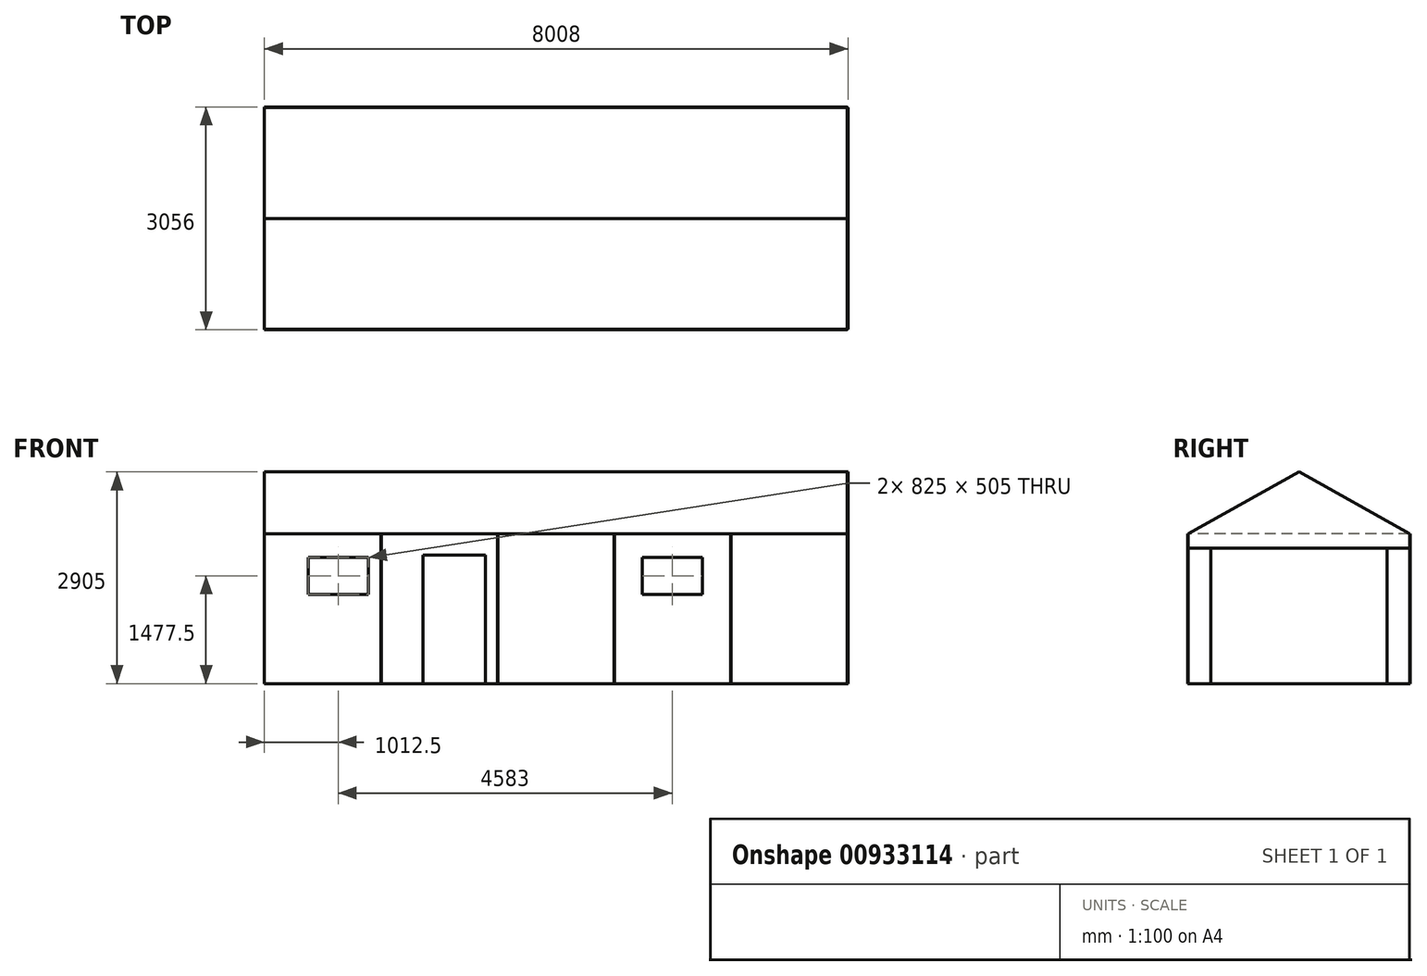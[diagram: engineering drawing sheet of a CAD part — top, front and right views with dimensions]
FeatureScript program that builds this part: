
annotation { "Feature Type Name" : "Feature", "Feature Type Description" : "" }
export const myFeature = defineFeature(function(context is Context, id is Id, definition is map)
    precondition{}
    {
        {
            var Q0;
            Q0=qCreatedBy(makeId("Top.planeOp"),FACE);
            var sketch = newSketch(context, id + "F0", { "sketchPlane" : qUnion([Q0])});
            skLineSegment(sketch, "E0.bottom", {"start": v(-4000, 1520) * mm, "end": v(4000, 1520) * mm});
            skLineSegment(sketch, "E0.top", {"start": v(-4000, -1520) * mm, "end": v(4000, -1520) * mm});
            skLineSegment(sketch, "E0.left", {"start": v(-4000, 1520) * mm, "end": v(-4000, -1520) * mm});
            skLineSegment(sketch, "E0.right", {"start": v(4000, 1520) * mm, "end": v(4000, -1520) * mm});
            skPoint(sketch, "E0.middle", {"position": v(0, 0) * mm});
            skSolve(sketch);
        }
        {
            var Q0;
            Q0 = qSketchRegion(id + "F0", true);
            extrude(context, id + "F1", {"entities" : qUnion([Q0]), "depth" : 2055 * mm, "offsetDistance" : 25 * mm});
        }
        {
            var Q0;
            Q0=makeQuery(id+"F1.opExtrude","SWEPT_FACE",FACE,{"disambiguationData":[OSD([sQuery(id+"F0.wireOp",EDGE,"E0.top")])]});
            var sketch = newSketch(context, id + "F2", { "sketchPlane" : qUnion([Q0])});
            skLineSegment(sketch, "E1.bottom", {"start": v(4000, 0) * mm, "end": v(2404, 0) * mm});
            skLineSegment(sketch, "E1.top", {"start": v(4000, 2055) * mm, "end": v(2404, 2055) * mm});
            skLineSegment(sketch, "E1.left", {"start": v(4000, 0) * mm, "end": v(4000, 2055) * mm});
            skLineSegment(sketch, "E1.right", {"start": v(2404, 0) * mm, "end": v(2404, 2055) * mm});
            skLineSegment(sketch, "E2.bottom", {"start": v(2399, 0) * mm, "end": v(803, 0) * mm});
            skLineSegment(sketch, "E2.top", {"start": v(2399, 2055) * mm, "end": v(803, 2055) * mm});
            skLineSegment(sketch, "E2.left", {"start": v(2399, 0) * mm, "end": v(2399, 2055) * mm});
            skLineSegment(sketch, "E2.right", {"start": v(803, 0) * mm, "end": v(803, 2055) * mm});
            skLineSegment(sketch, "E3.bottom", {"start": v(798, 0) * mm, "end": v(-798, 0) * mm});
            skLineSegment(sketch, "E3.top", {"start": v(798, 2055) * mm, "end": v(-798, 2055) * mm});
            skLineSegment(sketch, "E3.left", {"start": v(798, 0) * mm, "end": v(798, 2055) * mm});
            skLineSegment(sketch, "E3.right", {"start": v(-798, 0) * mm, "end": v(-798, 2055) * mm});
            skLineSegment(sketch, "E4.bottom", {"start": v(-803, 0) * mm, "end": v(-2399, 0) * mm});
            skLineSegment(sketch, "E4.top", {"start": v(-803, 2055) * mm, "end": v(-2399, 2055) * mm});
            skLineSegment(sketch, "E4.left", {"start": v(-803, 0) * mm, "end": v(-803, 2055) * mm});
            skLineSegment(sketch, "E4.right", {"start": v(-2399, 0) * mm, "end": v(-2399, 2055) * mm});
            skLineSegment(sketch, "E5.bottom", {"start": v(-2404, 0) * mm, "end": v(-4000, 0) * mm});
            skLineSegment(sketch, "E5.top", {"start": v(-2404, 2055) * mm, "end": v(-4000, 2055) * mm});
            skLineSegment(sketch, "E5.left", {"start": v(-2404, 0) * mm, "end": v(-2404, 2055) * mm});
            skLineSegment(sketch, "E5.right", {"start": v(-4000, 0) * mm, "end": v(-4000, 2055) * mm});
            skSolve(sketch);
        }
        {
            var Q0;
            Q0 = qSketchRegion(id + "F2", true);
            extrude(context, id + "F3", {"entities" : qUnion([Q0]), "depth" : 8 * mm, "offsetDistance" : 25 * mm});
        }
        {
            var Q0;
            Q0=makeQuery(id+"F1.opExtrude","SWEPT_FACE",FACE,{"disambiguationData":[OSD([sQuery(id+"F0.wireOp",EDGE,"E0.right")])]});
            var sketch = newSketch(context, id + "F4", { "sketchPlane" : qUnion([Q0])});
            skLineSegment(sketch, "E6.bottom", {"start": v(-1520, 0) * mm, "end": v(-1210, 0) * mm});
            skLineSegment(sketch, "E6.top", {"start": v(-1520, 1860) * mm, "end": v(-1210, 1860) * mm});
            skLineSegment(sketch, "E6.left", {"start": v(-1520, 0) * mm, "end": v(-1520, 1860) * mm});
            skLineSegment(sketch, "E6.right", {"start": v(-1210, 0) * mm, "end": v(-1210, 1860) * mm});
            skLineSegment(sketch, "E7.bottom", {"start": v(1520, 0) * mm, "end": v(1210, 0) * mm});
            skLineSegment(sketch, "E7.top", {"start": v(1520, 1860) * mm, "end": v(1210, 1860) * mm});
            skLineSegment(sketch, "E7.left", {"start": v(1520, 0) * mm, "end": v(1520, 1860) * mm});
            skLineSegment(sketch, "E7.right", {"start": v(1210, 0) * mm, "end": v(1210, 1860) * mm});
            skSolve(sketch);
        }
        {
            var Q0;
            Q0 = qSketchRegion(id + "F4", true);
            extrude(context, id + "F5", {"entities" : qUnion([Q0]), "depth" : 8 * mm, "offsetDistance" : 25 * mm});
        }
        {
            var Q0;
            Q0=makeQuery(id+"F1.opExtrude","SWEPT_FACE",FACE,{"disambiguationData":[OSD([sQuery(id+"F0.wireOp",EDGE,"E0.bottom")])]});
            var sketch = newSketch(context, id + "F6", { "sketchPlane" : qUnion([Q0])});
            skLineSegment(sketch, "E8.bottom", {"start": v(-4000, 0) * mm, "end": v(-2404, 0) * mm});
            skLineSegment(sketch, "E8.top", {"start": v(-4000, 2055) * mm, "end": v(-2404, 2055) * mm});
            skLineSegment(sketch, "E8.left", {"start": v(-4000, 0) * mm, "end": v(-4000, 2055) * mm});
            skLineSegment(sketch, "E8.right", {"start": v(-2404, 0) * mm, "end": v(-2404, 2055) * mm});
            skLineSegment(sketch, "E9.bottom", {"start": v(-2399, 0) * mm, "end": v(-803, 0) * mm});
            skLineSegment(sketch, "E9.top", {"start": v(-2399, 2055) * mm, "end": v(-803, 2055) * mm});
            skLineSegment(sketch, "E9.left", {"start": v(-2399, 0) * mm, "end": v(-2399, 2055) * mm});
            skLineSegment(sketch, "E9.right", {"start": v(-803, 0) * mm, "end": v(-803, 2055) * mm});
            skLineSegment(sketch, "E10.bottom", {"start": v(-798, 0) * mm, "end": v(798, 0) * mm});
            skLineSegment(sketch, "E10.top", {"start": v(-798, 2055) * mm, "end": v(798, 2055) * mm});
            skLineSegment(sketch, "E10.left", {"start": v(-798, 0) * mm, "end": v(-798, 2055) * mm});
            skLineSegment(sketch, "E10.right", {"start": v(798, 0) * mm, "end": v(798, 2055) * mm});
            skLineSegment(sketch, "E11.bottom", {"start": v(803, 0) * mm, "end": v(2399, 0) * mm});
            skLineSegment(sketch, "E11.top", {"start": v(803, 2055) * mm, "end": v(2399, 2055) * mm});
            skLineSegment(sketch, "E11.left", {"start": v(803, 0) * mm, "end": v(803, 2055) * mm});
            skLineSegment(sketch, "E11.right", {"start": v(2399, 0) * mm, "end": v(2399, 2055) * mm});
            skLineSegment(sketch, "E12.bottom", {"start": v(2404, 0) * mm, "end": v(4000, 0) * mm});
            skLineSegment(sketch, "E12.top", {"start": v(2404, 2055) * mm, "end": v(4000, 2055) * mm});
            skLineSegment(sketch, "E12.left", {"start": v(2404, 0) * mm, "end": v(2404, 2055) * mm});
            skLineSegment(sketch, "E12.right", {"start": v(4000, 0) * mm, "end": v(4000, 2055) * mm});
            skSolve(sketch);
        }
        {
            var Q0;
            Q0 = qSketchRegion(id + "F6", true);
            extrude(context, id + "F7", {"entities" : qUnion([Q0]), "depth" : 8 * mm, "offsetDistance" : 25 * mm});
        }
        {
            var Q0;
            {var subQ0=sQuery(id+"F2.wireOp",EDGE,"E3.right");Q0=makeQuery(id+"F2.imprint","IMPRINT",FACE,{"disambiguationData":[TD([[makeQuery(id+"F2.imprint","IMPRINT",EDGE,{"derivedFrom":subQ0}),1.0]])]});}
            var sketch = newSketch(context, id + "F8", { "sketchPlane" : qUnion([Q0])});
            skLineSegment(sketch, "E13.bottom", {"start": v(1183, 1730) * mm, "end": v(2008, 1730) * mm});
            skLineSegment(sketch, "E13.top", {"start": v(1183, 1225) * mm, "end": v(2008, 1225) * mm});
            skLineSegment(sketch, "E13.left", {"start": v(1183, 1730) * mm, "end": v(1183, 1225) * mm});
            skLineSegment(sketch, "E13.right", {"start": v(2008, 1730) * mm, "end": v(2008, 1225) * mm});
            skLineSegment(sketch, "E14.bottom", {"start": v(-3400, 1730) * mm, "end": v(-2575, 1730) * mm});
            skLineSegment(sketch, "E14.top", {"start": v(-3400, 1225) * mm, "end": v(-2575, 1225) * mm});
            skLineSegment(sketch, "E14.left", {"start": v(-3400, 1730) * mm, "end": v(-3400, 1225) * mm});
            skLineSegment(sketch, "E14.right", {"start": v(-2575, 1730) * mm, "end": v(-2575, 1225) * mm});
            skLineSegment(sketch, "E15.bottom", {"start": v(-1825, -35) * mm, "end": v(-965, -35) * mm});
            skLineSegment(sketch, "E15.top", {"start": v(-1825, 1765) * mm, "end": v(-965, 1765) * mm});
            skLineSegment(sketch, "E15.left", {"start": v(-1825, -35) * mm, "end": v(-1825, 1765) * mm});
            skLineSegment(sketch, "E15.right", {"start": v(-965, -35) * mm, "end": v(-965, 1765) * mm});
            skSolve(sketch);
        }
        {
            var Q0;
            Q0 = qSketchRegion(id + "F8", true);
            extrude(context, id + "F9", {"entities" : qUnion([Q0]), "operationType" : NewBodyOperationType.REMOVE, "depth" : 8 * mm, "offsetDistance" : 25 * mm});
        }
        {
            var Q0;
            Q0=makeQuery(id+"F1.opExtrude","CAP_FACE",FACE,{"disambiguationData":[OSD([sQuery(id+"F0.wireOp",EDGE,"E0.bottom"),sQuery(id+"F0.wireOp",EDGE,"E0.top"),sQuery(id+"F0.wireOp",EDGE,"E0.left"),sQuery(id+"F0.wireOp",EDGE,"E0.right")])],"isStart":false});
            extrude(context, id + "F10", {"entities" : qUnion([Q0]), "depth" : 850 * mm, "offsetDistance" : 25 * mm});
        }
        {
            var Q0;
            Q0=makeQuery(id+"F10.opExtrude","CAP_EDGE",EDGE,{"disambiguationData":[OSD([sQuery(id+"F0.wireOp",EDGE,"E0.top")])],"isStart":false});
            var Q1;
            Q1=makeQuery(id+"F10.opExtrude","CAP_EDGE",EDGE,{"disambiguationData":[OSD([sQuery(id+"F0.wireOp",EDGE,"E0.bottom")])],"isStart":false});
            chamfer(context, id + "F11", {"entities" : qUnion([Q0, Q1]), "chamferType" : ChamferType.TWO_OFFSETS, "width1" : 1520 * mm, "oppositeDirection" : false, "width2" : 850 * mm, "tangentPropagation" : true});
        }
        {
            var Q0;
            Q0=makeQuery(id+"F1.opExtrude","SWEPT_FACE",FACE,{"disambiguationData":[OSD([sQuery(id+"F0.wireOp",EDGE,"E0.right")])]});
            var sketch = newSketch(context, id + "F12", { "sketchPlane" : qUnion([Q0])});
            skLineSegment(sketch, "E16.bottom", {"start": v(-1520, 1860) * mm, "end": v(1520, 1860) * mm});
            skLineSegment(sketch, "E16.top", {"start": v(-1520, 2905) * mm, "end": v(1520, 2905) * mm});
            skLineSegment(sketch, "E16.left", {"start": v(-1520, 1860) * mm, "end": v(-1520, 2905) * mm});
            skLineSegment(sketch, "E16.right", {"start": v(1520, 1860) * mm, "end": v(1520, 2905) * mm});
            skSolve(sketch);
        }
        {
            var Q0;
            Q0 = qSketchRegion(id + "F12", true);
            extrude(context, id + "F13", {"entities" : qUnion([Q0]), "depth" : 8 * mm, "offsetDistance" : 25 * mm});
        }
        {
            var Q0;
            Q0=makeQuery(id+"F13.opExtrude","SWEPT_EDGE",EDGE,{"disambiguationData":[OSD([sQuery(id+"F12.wireOp",EDGE,"E16.top"),sQuery(id+"F12.wireOp",EDGE,"E16.left")])]});
            var Q1;
            Q1=makeQuery(id+"F13.opExtrude","SWEPT_EDGE",EDGE,{"disambiguationData":[OSD([sQuery(id+"F12.wireOp",EDGE,"E16.top"),sQuery(id+"F12.wireOp",EDGE,"E16.right")])]});
            chamfer(context, id + "F14", {"entities" : qUnion([Q0, Q1]), "chamferType" : ChamferType.TWO_OFFSETS, "width1" : 850 * mm, "oppositeDirection" : false, "width2" : 1520 * mm, "tangentPropagation" : true});
        }
    });
